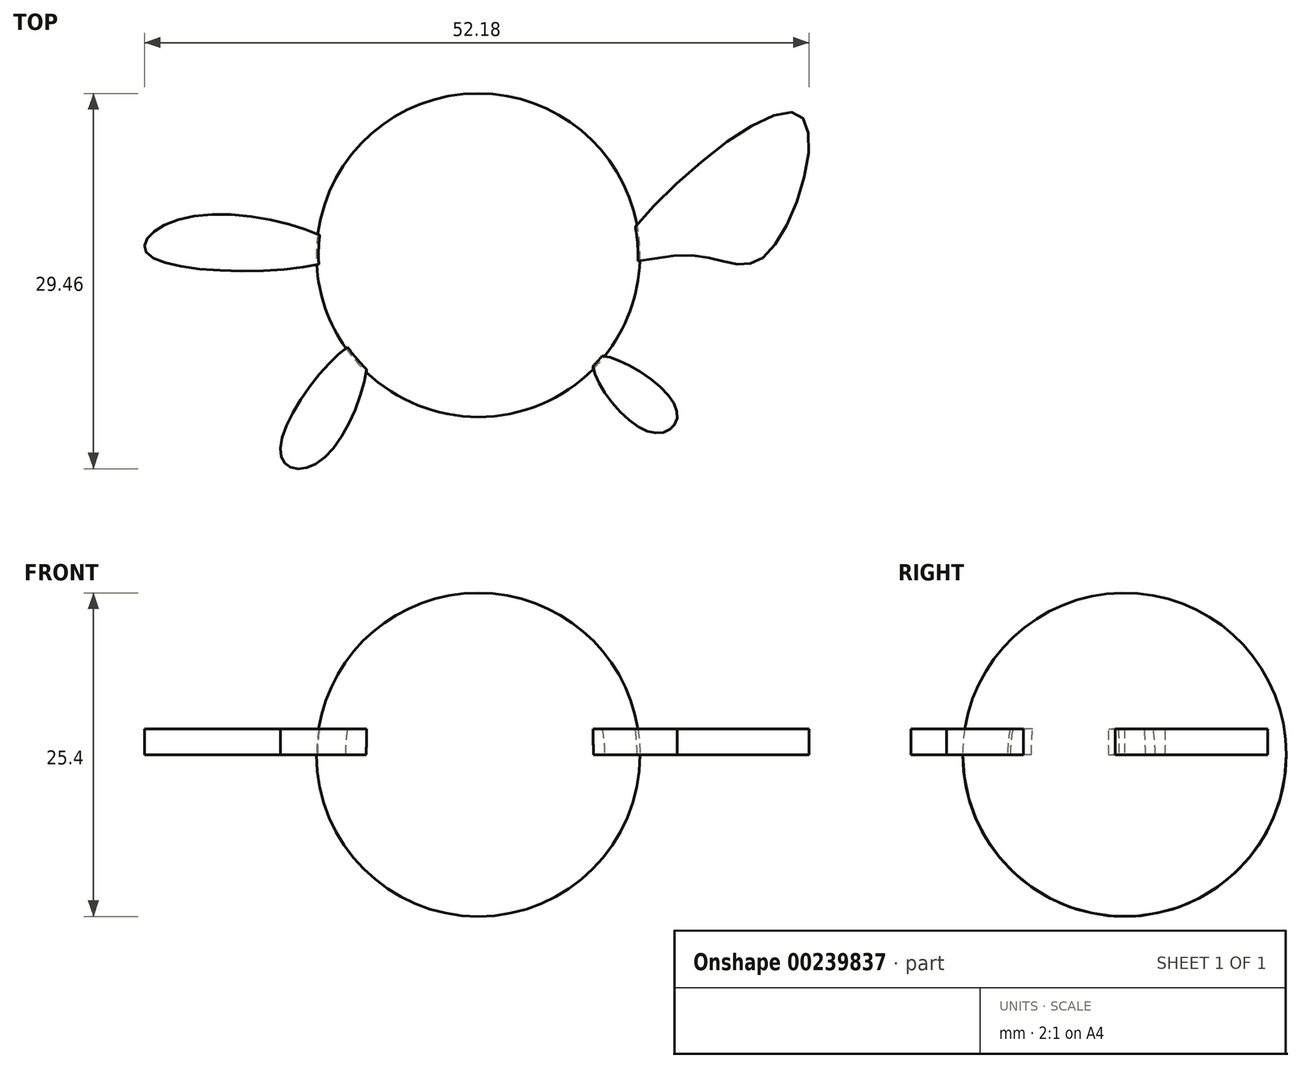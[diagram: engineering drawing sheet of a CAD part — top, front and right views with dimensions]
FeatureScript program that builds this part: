
annotation { "Feature Type Name" : "Feature", "Feature Type Description" : "" }
export const myFeature = defineFeature(function(context is Context, id is Id, definition is map)
    precondition{}
    {
        {
            var Q0;
            Q0=qCreatedBy(makeId("Top.planeOp"),FACE);
            var sketch = newSketch(context, id + "F0", { "sketchPlane" : qUnion([Q0])});
            skCircle(sketch, "E0", {"center": v(0, 0) * mm, "radius": 12.7 * mm});
            skLineSegment(sketch, "E1", {"start": v(0, 12.7) * mm, "end": v(0, -12.7) * mm});
            skSolve(sketch);
        }
        {
            var Q0;
            {var subQ0=sQuery(id+"F0.wireOp",EDGE,"E1");Q0=makeQuery(id+"F0.imprint","IMPRINT",FACE,{"disambiguationData":[TD([[makeQuery(id+"F0.imprint","IMPRINT",EDGE,{"derivedFrom":subQ0}),-1.0]])]});}
            var Q1;
            Q1=sQuery(id+"F0.wireOp",EDGE,"E1");
            revolve(context, id + "F1", {"entities" : qUnion([Q0]), "axis" : qUnion([Q1]), "revolveType" : RevolveType.FULL});
        }
        {
            var Q0;
            Q0=qCreatedBy(makeId("Top.planeOp"),FACE);
            var sketch = newSketch(context, id + "F2", { "sketchPlane" : qUnion([Q0])});
            skFitSpline(sketch, "E2", {"points": [v(11, 0) * mm, v(24.95, 11.14) * mm, v(22.56, 0) * mm, v(16.56, 0) * mm, v(11, 0) * mm]});
            skFitSpline(sketch, "E3", {"points": [v(-11, 0) * mm, v(-21.98, 3.12) * mm, v(-25.85, 0) * mm, v(-11, 0) * mm]});
            skSolve(sketch);
        }
        {
            var Q0;
            Q0=qCreatedBy(makeId("Top.planeOp"),FACE);
            var sketch = newSketch(context, id + "F3", { "sketchPlane" : qUnion([Q0])});
            skFitSpline(sketch, "E4", {"points": [v(-9.14, -6.86) * mm, v(-15.54, -15.4) * mm, v(-12.2, -16) * mm, v(-9.14, -6.86) * mm]});
            skFitSpline(sketch, "E5", {"points": [v(9.14, -8.08) * mm, v(13.41, -13.87) * mm, v(15.54, -12.04) * mm, v(9.14, -8.08) * mm]});
            skSolve(sketch);
        }
        {
            var Q0;
            Q0=qCreatedBy(makeId("Top.planeOp"),FACE);
            var sketch = newSketch(context, id + "F4", { "sketchPlane" : qUnion([Q0])});
            skSolve(sketch);
        }
        {
            var Q0;
            Q0 = qSketchRegion(id + "F4", true);
            var Q1;
            Q1=makeQuery(id+"F2.imprint","IMPRINT",FACE,{"disambiguationData":[TD([[makeQuery(id+"F2.imprint","IMPRINT",EDGE,{"derivedFrom":sQuery(id+"F2.wireOp",EDGE,"E3")}),1.0]])]});
            var Q2;
            Q2=makeQuery(id+"F3.imprint","IMPRINT",FACE,{"disambiguationData":[TD([[makeQuery(id+"F3.imprint","IMPRINT",EDGE,{"derivedFrom":sQuery(id+"F3.wireOp",EDGE,"E4")}),1.0]])]});
            var Q3;
            Q3=makeQuery(id+"F3.imprint","IMPRINT",FACE,{"disambiguationData":[TD([[makeQuery(id+"F3.imprint","IMPRINT",EDGE,{"derivedFrom":sQuery(id+"F3.wireOp",EDGE,"E5")}),1.0]])]});
            var Q4;
            Q4=makeQuery(id+"F2.imprint","IMPRINT",FACE,{"disambiguationData":[TD([[makeQuery(id+"F2.imprint","IMPRINT",EDGE,{"derivedFrom":sQuery(id+"F2.wireOp",EDGE,"E2")}),-1.0]])]});
            extrude(context, id + "F5", {"entities" : qUnion([Q0, Q1, Q2, Q3, Q4]), "operationType" : NewBodyOperationType.ADD, "depth" : 2.03 * mm});
        }
    });
